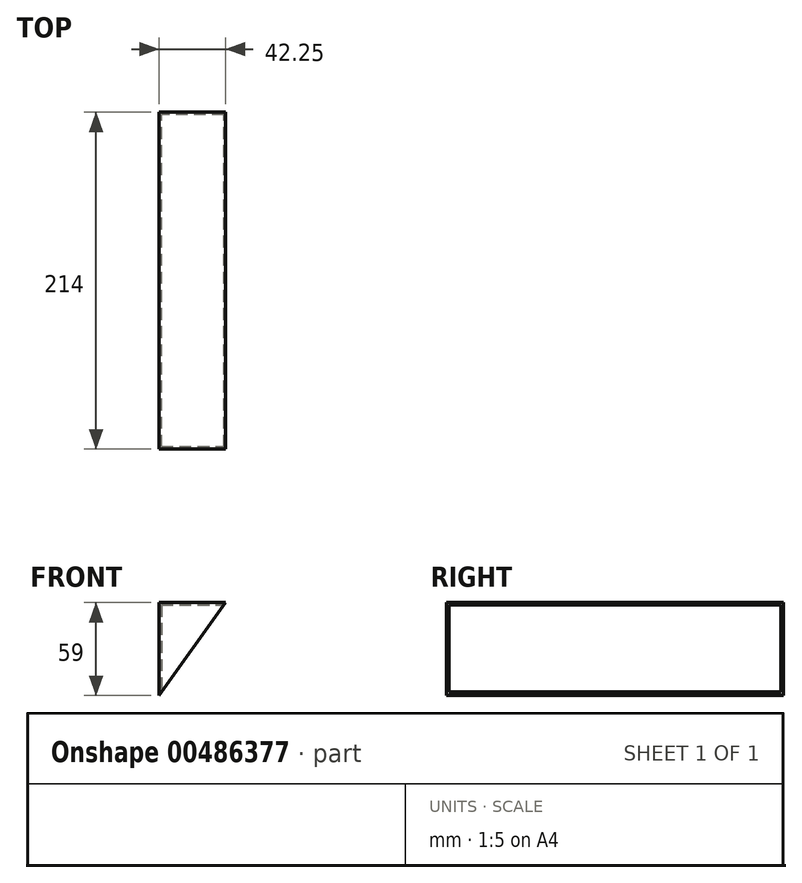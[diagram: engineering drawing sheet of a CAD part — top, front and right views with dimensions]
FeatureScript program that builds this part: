
annotation { "Feature Type Name" : "Feature", "Feature Type Description" : "" }
export const myFeature = defineFeature(function(context is Context, id is Id, definition is map)
    precondition{}
    {
        {
            var Q0;
            Q0=qCreatedBy(makeId("Top.planeOp"),FACE);
            var sketch = newSketch(context, id + "F0", { "sketchPlane" : qUnion([Q0])});
            skLineSegment(sketch, "E0.bottom", {"start": v(0, 0) * mm, "end": v(42.25, 0) * mm});
            skLineSegment(sketch, "E0.top", {"start": v(0, 214) * mm, "end": v(42.25, 214) * mm});
            skLineSegment(sketch, "E0.left", {"start": v(0, 0) * mm, "end": v(0, 214) * mm});
            skLineSegment(sketch, "E0.right", {"start": v(42.25, 0) * mm, "end": v(42.25, 214) * mm});
            skSolve(sketch);
        }
        {
            var Q0;
            Q0=makeQuery(id+"F0.imprint","IMPRINT",FACE,{"disambiguationData":[TD([[makeQuery(id+"F0.imprint","IMPRINT",EDGE,{"derivedFrom":sQuery(id+"F0.wireOp",EDGE,"E0.bottom")}),1.0]])]});
            extrude(context, id + "F1", {"entities" : qUnion([Q0]), "depth" : 59 * mm});
        }
        {
            var Q0;
            Q0=makeQuery(id+"F1.opExtrude","SWEPT_FACE",FACE,{"disambiguationData":[OSD([sQuery(id+"F0.wireOp",EDGE,"E0.top")])]});
            var sketch = newSketch(context, id + "F2", { "sketchPlane" : qUnion([Q0])});
            skLineSegment(sketch, "E1", {"start": v(-42.25, 59) * mm, "end": v(0, 0) * mm});
            skSolve(sketch);
        }
        {
            var Q0;
            Q0=makeQuery(id+"F2.imprint","IMPRINT",FACE,{"disambiguationData":[TD([[makeQuery(id+"F2.imprint","IMPRINT",EDGE,{"derivedFrom":sQuery(id+"F2.wireOp",EDGE,"E1")}),-1.0]])]});
            extrude(context, id + "F3", {"entities" : qUnion([Q0]), "operationType" : NewBodyOperationType.REMOVE, "endBound" : BoundingType.UP_TO_NEXT, "oppositeDirection" : true, "depth" : 25 * mm});
        }
        {
            var Q0;
            Q0=makeQuery(id+"F3.boolean.opBoolean","COPY",FACE,{"derivedFrom":makeQuery(id+"F3.opExtrude","SWEPT_FACE",FACE,{"disambiguationData":[OSD([sQuery(id+"F2.wireOp",EDGE,"E1")])]})});
            shell(context, id + "F4", {"entities" : qUnion([Q0]), "thickness" : 1.5 * mm});
        }
    });
